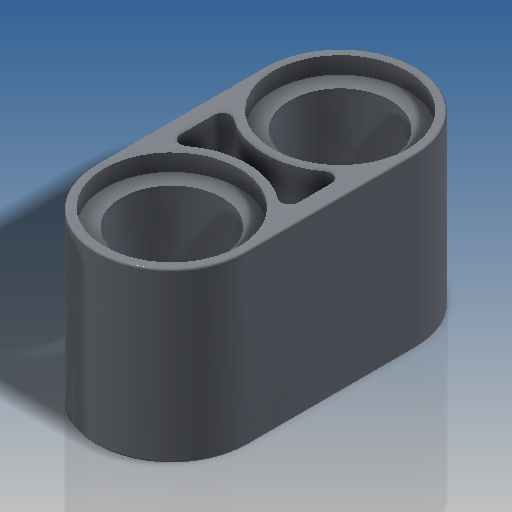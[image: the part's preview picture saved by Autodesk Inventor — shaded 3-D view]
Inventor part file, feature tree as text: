
AUTODESK INVENTOR PART (.ipt)
format: ipt  version: 2018.3 (Build 223284000, 284)  size: 257,024 bytes
history: native  units: mm
features: extrude x3, sketch x2, mirror x1, fillet x1
ambient origin geometry x8: Origin, YZ Plane, XZ Plane, XY Plane, X Axis, Y Axis, Z Axis, Center Point
bodies: Solid1 (feature_tree)
feature tree (7):
  extrude  "Extrusion1"  Depth=6.4mm
  sketch  "Sketch6"  dims[d14=8.0mm d15=0.0mm d32=7.2mm d34=8.0mm d36=0.8mm d41=0.8mm d42=0.0mm d43=3.1mm d44=0.0mm d45=0.1mm d46=0.4mm]
  extrude  "Extrusion7"  Depth=7.2mm
  extrude  "Extrusion8"  Depth=8.0mm
  mirror  "Mirror1"
  fillet  "Fillet1"  Radius=0.8mm
  sketch  "Sketch1"  dims[d8=4.8mm d9=6.4mm]
